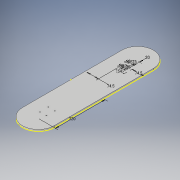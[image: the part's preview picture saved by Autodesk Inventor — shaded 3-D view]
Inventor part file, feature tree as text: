
AUTODESK INVENTOR PART (.ipt)
format: ipt  version: 2019 (Build 230136000, 136)  size: 131,072 bytes
history: native  units: mm
features: sketch x3, hole x2, other x1, extrude x1
ambient origin geometry x8: Origin, YZ Plane, XZ Plane, XY Plane, X Axis, Y Axis, Z Axis, Center Point
bodies: Body1 (feature_tree)
feature tree (7):
  other  "ソリッド1"
  sketch  "スケッチ1"
  extrude  "押し出し1"  Depth=270.0mm
  sketch  "スケッチ4"
  hole  "穴2"  [1 undecoded]
  hole  "穴3"  [1 undecoded]
  sketch  "スケッチ2"
note: 2 required parameter values undecoded (feature->parameter linkage not recoverable at this tier; creation-order binding heuristic only, values carry confidence <= 0.55)
